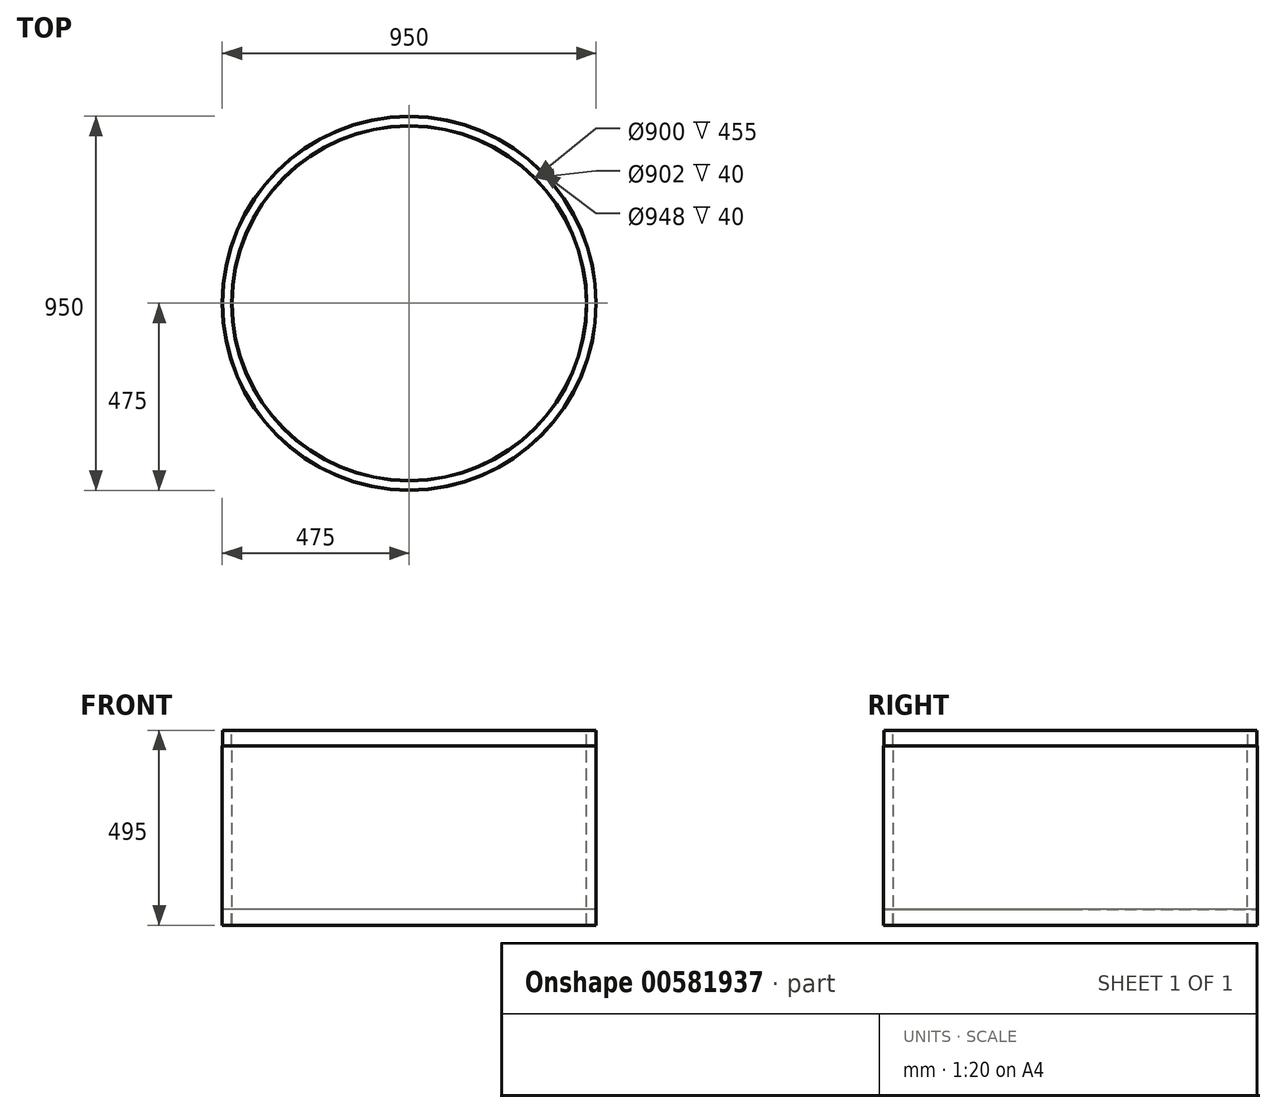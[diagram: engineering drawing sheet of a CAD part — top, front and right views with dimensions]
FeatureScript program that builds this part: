
annotation { "Feature Type Name" : "Feature", "Feature Type Description" : "" }
export const myFeature = defineFeature(function(context is Context, id is Id, definition is map)
    precondition{}
    {
        {
            var Q0;
            Q0=qCreatedBy(makeId("Front.planeOp"),FACE);
            var sketch = newSketch(context, id + "F0", { "sketchPlane" : qUnion([Q0])});
            skLineSegment(sketch, "E0", {"start": v(0, 345.75) * mm, "end": v(0, -558.03) * mm, "construction": true});
            skLineSegment(sketch, "E1", {"start": v(-450, -518.84) * mm, "end": v(-450, -63.84) * mm});
            skLineSegment(sketch, "E2", {"start": v(-450, -63.84) * mm, "end": v(-451, -63.84) * mm});
            skLineSegment(sketch, "E3", {"start": v(-451, -63.84) * mm, "end": v(-451, -23.84) * mm});
            skLineSegment(sketch, "E4", {"start": v(-451, -23.84) * mm, "end": v(-474, -23.84) * mm});
            skLineSegment(sketch, "E5", {"start": v(-474, -23.84) * mm, "end": v(-474, -63.84) * mm});
            skLineSegment(sketch, "E6", {"start": v(-474, -63.84) * mm, "end": v(-475, -63.84) * mm});
            skLineSegment(sketch, "E7", {"start": v(-475, -63.84) * mm, "end": v(-475, -518.84) * mm});
            skLineSegment(sketch, "E8", {"start": v(-475, -518.84) * mm, "end": v(-474, -518.84) * mm});
            skLineSegment(sketch, "E9", {"start": v(-474, -518.84) * mm, "end": v(-474, -478.84) * mm});
            skLineSegment(sketch, "E10", {"start": v(-474, -478.84) * mm, "end": v(-451, -478.84) * mm});
            skLineSegment(sketch, "E11", {"start": v(-451, -478.84) * mm, "end": v(-451, -518.84) * mm});
            skLineSegment(sketch, "E12", {"start": v(-451, -518.84) * mm, "end": v(-450, -518.84) * mm});
            skSolve(sketch);
        }
        {
            var Q0;
            Q0=qSketchRegion(id+"F0",true);
            var Q1;
            Q1=sQuery(id+"F0.wireOp",EDGE,"E0");
            revolve(context, id + "F1", {"entities" : qUnion([Q0]), "axis" : qUnion([Q1]), "revolveType" : RevolveType.FULL});
        }
    });
